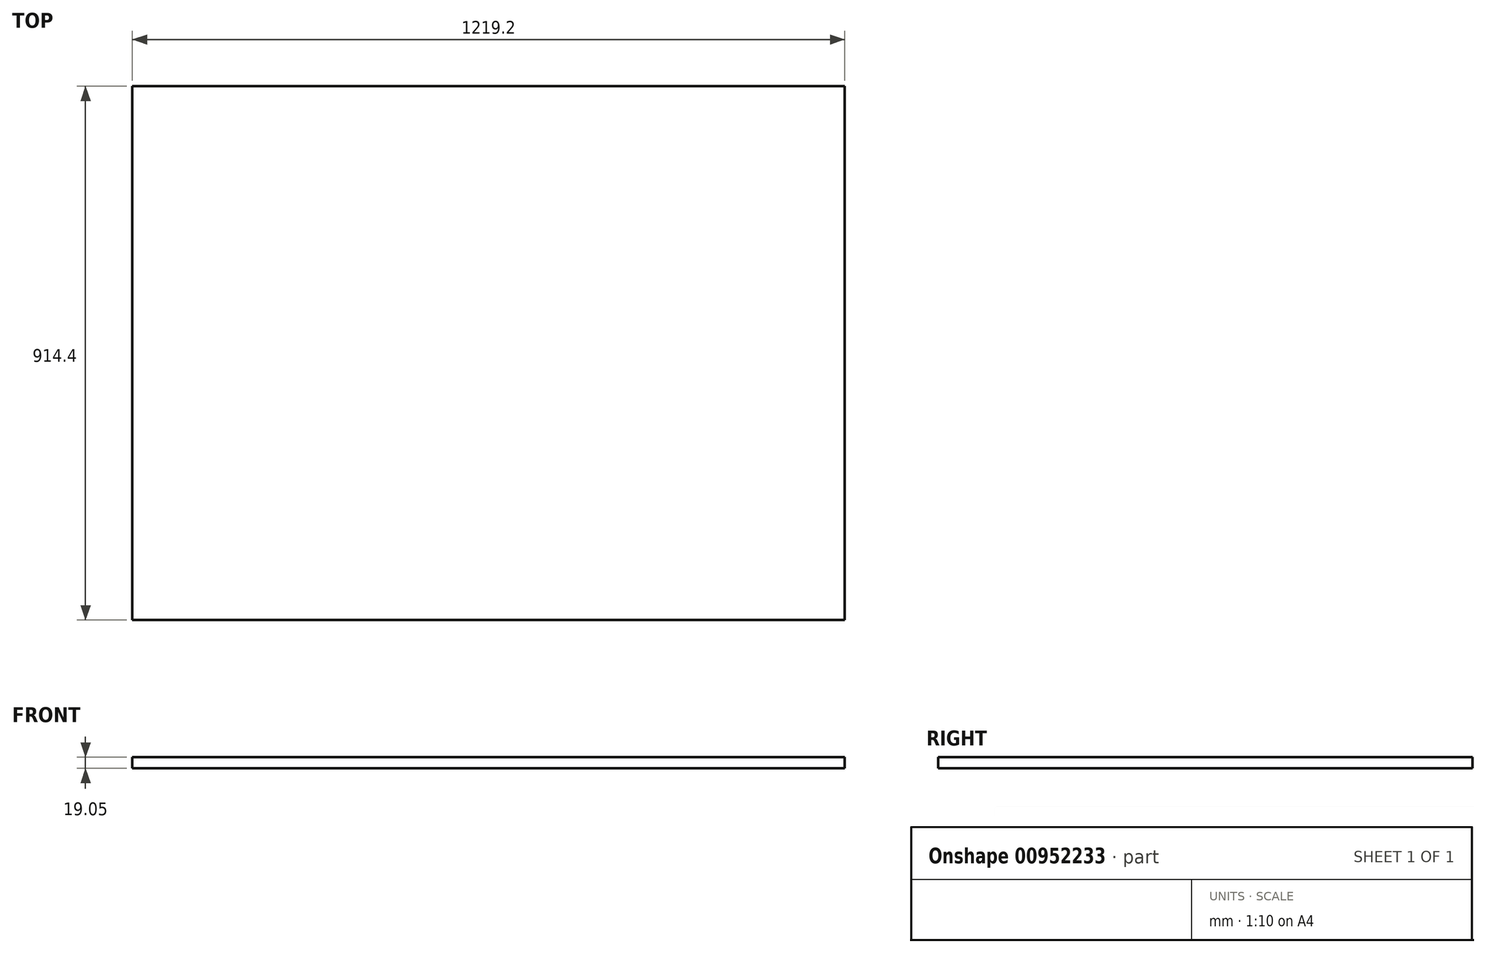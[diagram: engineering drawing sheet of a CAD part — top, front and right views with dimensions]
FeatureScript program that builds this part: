
annotation { "Feature Type Name" : "Feature", "Feature Type Description" : "" }
export const myFeature = defineFeature(function(context is Context, id is Id, definition is map)
    precondition{}
    {
        {
            var Q0;
            Q0=qCreatedBy(makeId("Front.planeOp"),FACE);
            var sketch = newSketch(context, id + "F0", { "sketchPlane" : qUnion([Q0])});
            skLineSegment(sketch, "E0.bottom", {"start": v(0, 0) * mm, "end": v(1219.2, 0) * mm});
            skLineSegment(sketch, "E0.top", {"start": v(0, -19.05) * mm, "end": v(1219.2, -19.05) * mm});
            skLineSegment(sketch, "E0.left", {"start": v(0, 0) * mm, "end": v(0, -19.05) * mm});
            skLineSegment(sketch, "E0.right", {"start": v(1219.2, 0) * mm, "end": v(1219.2, -19.05) * mm});
            skSolve(sketch);
        }
        {
            var Q0;
            Q0 = qSketchRegion(id + "F0", true);
            extrude(context, id + "F1", {"entities" : qUnion([Q0]), "depth" : 914.4 * mm, "offsetDistance" : 25.4 * mm});
        }
    });
